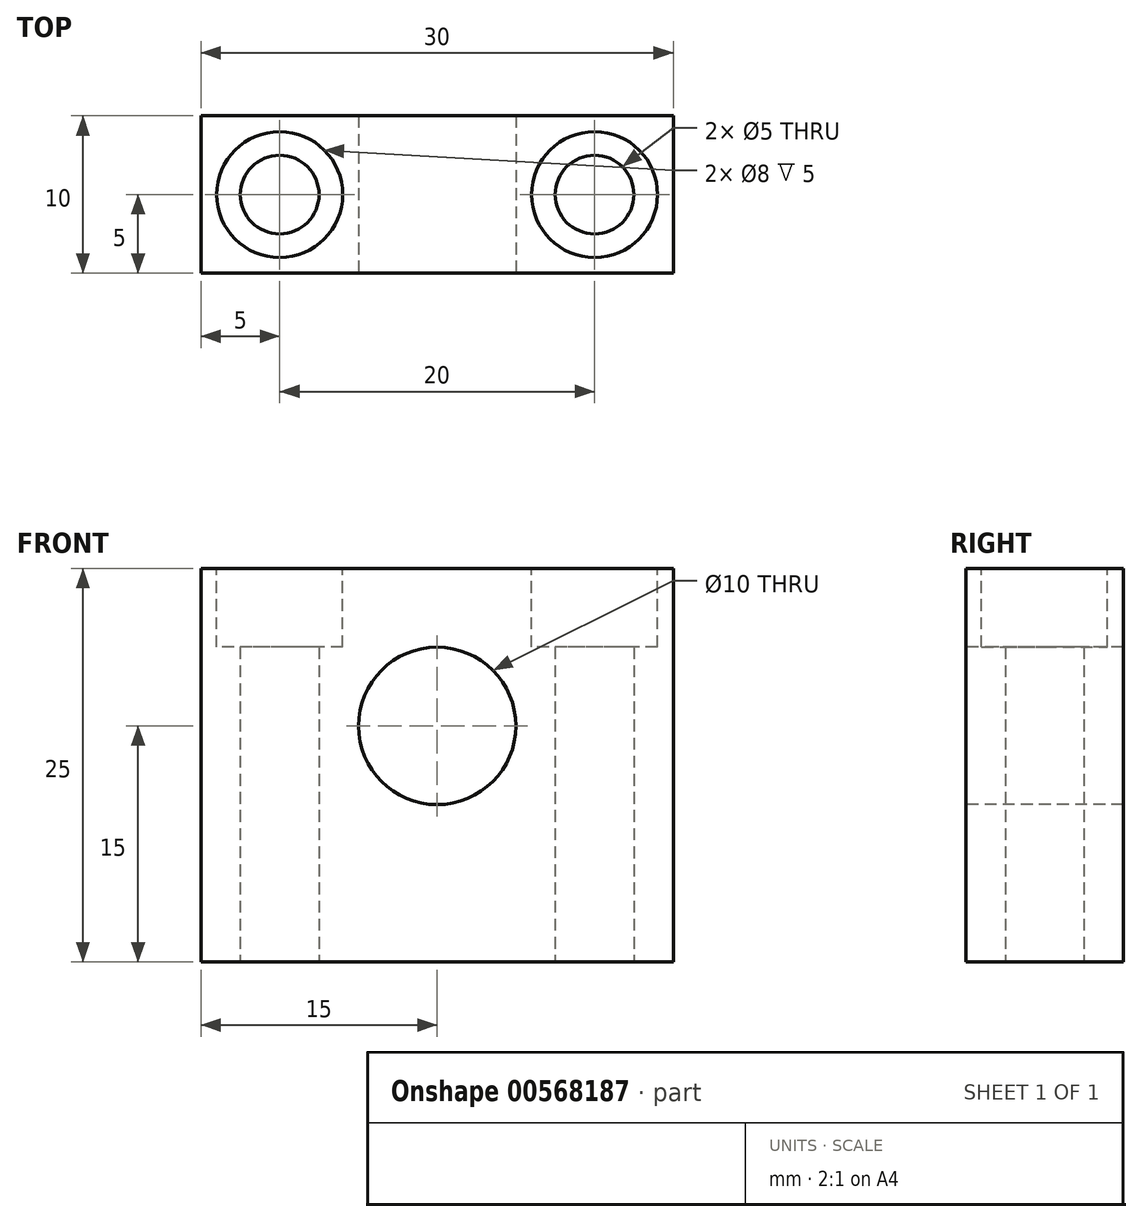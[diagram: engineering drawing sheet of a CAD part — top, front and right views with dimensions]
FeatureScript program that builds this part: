
annotation { "Feature Type Name" : "Feature", "Feature Type Description" : "" }
export const myFeature = defineFeature(function(context is Context, id is Id, definition is map)
    precondition{}
    {
        {
            var Q0;
            Q0=qCreatedBy(makeId("Top.planeOp"),FACE);
            var sketch = newSketch(context, id + "F0", { "sketchPlane" : qUnion([Q0])});
            skLineSegment(sketch, "E0.bottom", {"start": v(0, 0) * mm, "end": v(30, 0) * mm});
            skLineSegment(sketch, "E0.top", {"start": v(0, 10) * mm, "end": v(30, 10) * mm});
            skLineSegment(sketch, "E0.left", {"start": v(0, 0) * mm, "end": v(0, 10) * mm});
            skLineSegment(sketch, "E0.right", {"start": v(30, 0) * mm, "end": v(30, 10) * mm});
            skLineSegment(sketch, "E1", {"start": v(0, 5) * mm, "end": v(30, 5) * mm, "construction": true});
            skCircle(sketch, "E2", {"center": v(5, 5) * mm, "radius": 2.5 * mm});
            skCircle(sketch, "E3", {"center": v(25, 5) * mm, "radius": 2.5 * mm});
            skSolve(sketch);
        }
        {
            var Q0;
            Q0 = qSketchRegion(id + "F0", true);
            extrude(context, id + "F1", {"entities" : qUnion([Q0]), "depth" : 25 * mm, "offsetDistance" : 25 * mm});
        }
        {
            var Q0;
            Q0=makeQuery(id+"F1.opExtrude","CAP_FACE",FACE,{"disambiguationData":[OSD([sQuery(id+"F0.wireOp",EDGE,"E0.bottom"),sQuery(id+"F0.wireOp",EDGE,"E0.top"),sQuery(id+"F0.wireOp",EDGE,"E0.left"),sQuery(id+"F0.wireOp",EDGE,"E0.right"),sQuery(id+"F0.wireOp",EDGE,"E2"),sQuery(id+"F0.wireOp",EDGE,"E3")])],"isStart":false});
            var sketch = newSketch(context, id + "F2", { "sketchPlane" : qUnion([Q0])});
            skCircle(sketch, "E4", {"center": v(5, 5) * mm, "radius": 4 * mm});
            skCircle(sketch, "E5", {"center": v(25, 5) * mm, "radius": 4 * mm});
            skSolve(sketch);
        }
        {
            var Q0;
            Q0 = qSketchRegion(id + "F2", true);
            extrude(context, id + "F3", {"entities" : qUnion([Q0]), "operationType" : NewBodyOperationType.REMOVE, "oppositeDirection" : true, "depth" : 5 * mm, "offsetDistance" : 25 * mm});
        }
        {
            var Q0;
            Q0=makeQuery(id+"F1.opExtrude","SWEPT_FACE",FACE,{"disambiguationData":[OSD([sQuery(id+"F0.wireOp",EDGE,"E0.bottom")])]});
            var sketch = newSketch(context, id + "F4", { "sketchPlane" : qUnion([Q0])});
            skCircle(sketch, "E6", {"center": v(15, 15) * mm, "radius": 5 * mm});
            skSolve(sketch);
        }
        {
            var Q0;
            Q0 = qSketchRegion(id + "F4", true);
            extrude(context, id + "F5", {"entities" : qUnion([Q0]), "operationType" : NewBodyOperationType.REMOVE, "oppositeDirection" : true, "depth" : 25 * mm, "offsetDistance" : 25 * mm});
        }
    });
